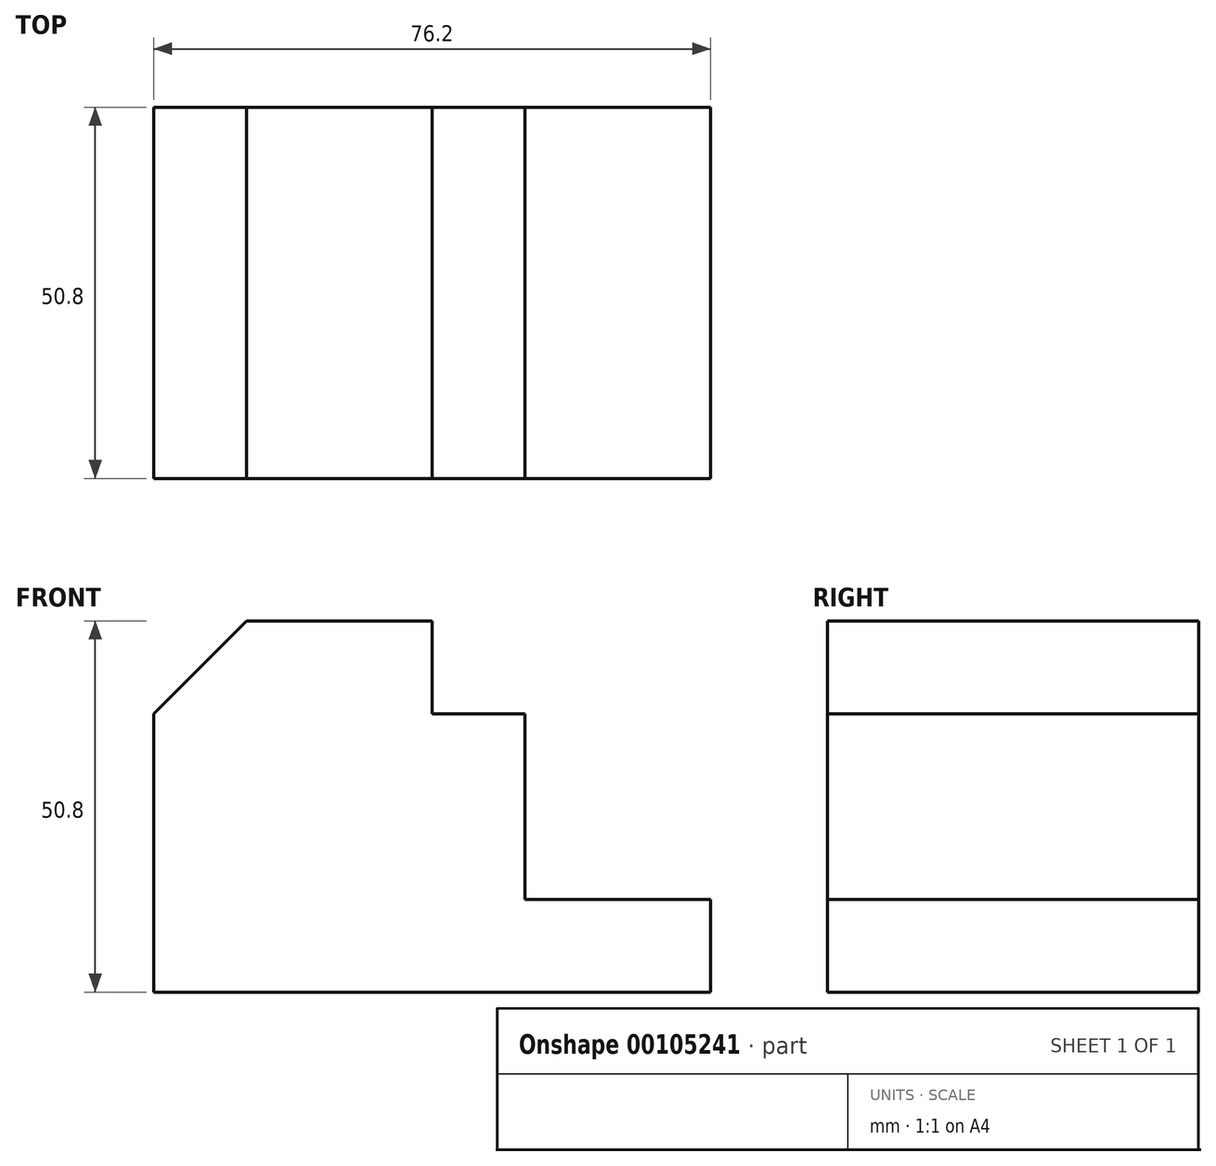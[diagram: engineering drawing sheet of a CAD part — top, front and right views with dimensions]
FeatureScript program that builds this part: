
annotation { "Feature Type Name" : "Feature", "Feature Type Description" : "" }
export const myFeature = defineFeature(function(context is Context, id is Id, definition is map)
    precondition{}
    {
        {
            var Q0;
            Q0=qCreatedBy(makeId("Front.planeOp"),FACE);
            var sketch = newSketch(context, id + "F0", { "sketchPlane" : qUnion([Q0])});
            skLineSegment(sketch, "E0", {"start": v(0, 0) * mm, "end": v(0, 38.1) * mm});
            skLineSegment(sketch, "E1", {"start": v(0, 38.1) * mm, "end": v(12.7, 50.8) * mm});
            skLineSegment(sketch, "E2", {"start": v(12.7, 50.8) * mm, "end": v(38.1, 50.8) * mm});
            skLineSegment(sketch, "E3", {"start": v(38.1, 50.8) * mm, "end": v(38.1, 38.1) * mm});
            skLineSegment(sketch, "E4", {"start": v(38.1, 38.1) * mm, "end": v(50.8, 38.1) * mm});
            skLineSegment(sketch, "E5", {"start": v(50.8, 38.1) * mm, "end": v(50.8, 12.7) * mm});
            skLineSegment(sketch, "E6", {"start": v(50.8, 12.7) * mm, "end": v(76.2, 12.7) * mm});
            skLineSegment(sketch, "E7", {"start": v(76.2, 12.7) * mm, "end": v(76.2, 0) * mm});
            skLineSegment(sketch, "E8", {"start": v(76.2, 0) * mm, "end": v(0, 0) * mm});
            skLineSegment(sketch, "E9", {"start": v(25.4, 50.8) * mm, "end": v(25.4, 25.4) * mm});
            skLineSegment(sketch, "E10", {"start": v(25.4, 25.4) * mm, "end": v(50.8, 25.4) * mm});
            skSolve(sketch);
        }
        {
            var Q0;
            Q0=makeQuery(id+"F0.imprint","IMPRINT",FACE,{"disambiguationData":[TD([[makeQuery(id+"F0.imprint","IMPRINT",EDGE,{"derivedFrom":sQuery(id+"F0.wireOp",EDGE,"E0")}),-1.0]])]});
            extrude(context, id + "F1", {"entities" : qUnion([Q0]), "endBound" : BoundingType.SYMMETRIC, "depth" : 50.8 * mm});
        }
        {
            var Q0;
            {var subQ3=sQuery(id+"F0.wireOp",EDGE,"E3");Q0=makeQuery(id+"F0.imprint","IMPRINT",FACE,{"disambiguationData":[TD([[makeQuery(id+"F0.imprint","IMPRINT",EDGE,{"derivedFrom":subQ3}),-1.0]])]});}
            var Q1;
            Q1 = qSketchRegion(id + "F6EEUMGAqokoA0w_1", true);
            extrude(context, id + "F2", {"entities" : qUnion([Q0, Q1]), "operationType" : NewBodyOperationType.ADD, "endBound" : BoundingType.SYMMETRIC, "depth" : 50.8 * mm});
        }
        {
            var Q0;
            {var subQ3=sQuery(id+"F0.wireOp",EDGE,"E3");Q0=makeQuery(id+"F0.imprint","IMPRINT",FACE,{"disambiguationData":[TD([[makeQuery(id+"F0.imprint","IMPRINT",EDGE,{"derivedFrom":subQ3}),-1.0]])]});}
            extrude(context, id + "F3", {"entities" : qUnion([Q0]), "operationType" : NewBodyOperationType.ADD, "endBound" : BoundingType.SYMMETRIC, "depth" : 25.4 * mm});
        }
    });
